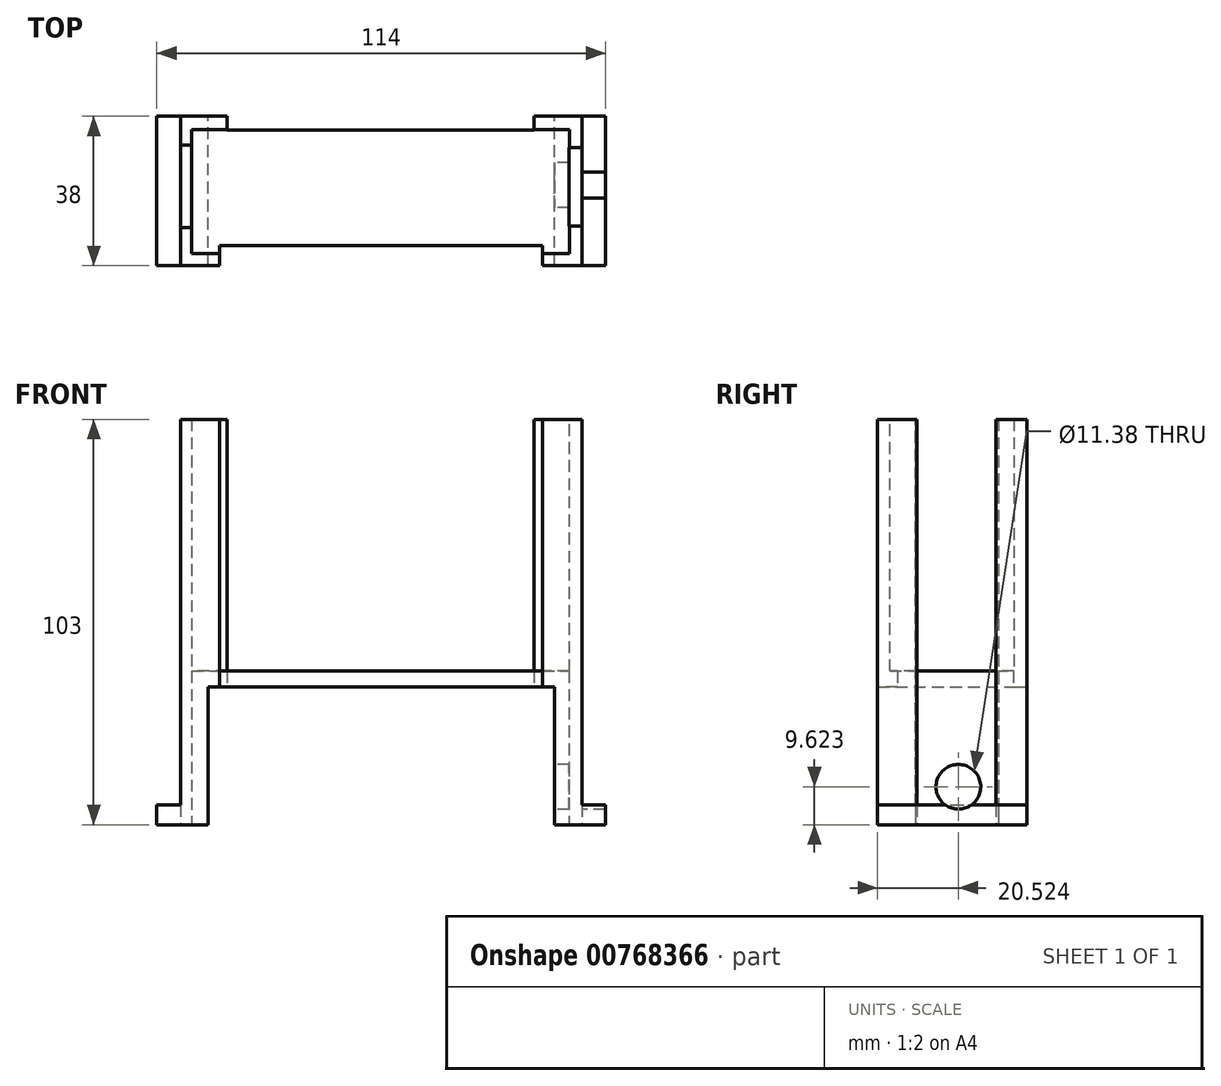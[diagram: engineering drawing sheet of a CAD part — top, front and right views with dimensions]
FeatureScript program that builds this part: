
annotation { "Feature Type Name" : "Feature", "Feature Type Description" : "" }
export const myFeature = defineFeature(function(context is Context, id is Id, definition is map)
    precondition{}
    {
        {
            var Q0;
            Q0=qCreatedBy(makeId("Front.planeOp"),FACE);
            var sketch = newSketch(context, id + "F0", { "sketchPlane" : qUnion([Q0])});
            skLineSegment(sketch, "E0", {"start": v(-44, 0) * mm, "end": v(-57, 0) * mm});
            skLineSegment(sketch, "E1", {"start": v(-57, 0) * mm, "end": v(-57, 5) * mm});
            skLineSegment(sketch, "E2", {"start": v(-57, 5) * mm, "end": v(-51, 5) * mm});
            skLineSegment(sketch, "E3", {"start": v(-51, 5) * mm, "end": v(-51, 103) * mm});
            skLineSegment(sketch, "E4", {"start": v(-51, 103) * mm, "end": v(0, 103) * mm});
            skLineSegment(sketch, "E5", {"start": v(-44, 0) * mm, "end": v(-44, 35) * mm});
            skLineSegment(sketch, "E6", {"start": v(-44, 35) * mm, "end": v(0, 35) * mm});
            skLineSegment(sketch, "E7", {"start": v(0, -35.05) * mm, "end": v(0, 128.52) * mm, "construction": true});
            skLineSegment(sketch, "E8.MirrorCS", {"start": v(51, 103) * mm, "end": v(0, 103) * mm});
            skLineSegment(sketch, "E9.MirrorCS", {"start": v(51, 5) * mm, "end": v(51, 103) * mm});
            skLineSegment(sketch, "E10.MirrorCS", {"start": v(44, 35) * mm, "end": v(0, 35) * mm});
            skLineSegment(sketch, "E11.MirrorCS", {"start": v(44, 0) * mm, "end": v(44, 35) * mm});
            skLineSegment(sketch, "E12.MirrorCS", {"start": v(57, 5) * mm, "end": v(51, 5) * mm});
            skLineSegment(sketch, "E13.MirrorCS", {"start": v(57, 0) * mm, "end": v(57, 5) * mm});
            skLineSegment(sketch, "E14.MirrorCS", {"start": v(44, 0) * mm, "end": v(57, 0) * mm});
            skSolve(sketch);
        }
        {
            var Q0;
            Q0 = qSketchRegion(id + "F0", true);
            extrude(context, id + "F1", {"entities" : qUnion([Q0]), "depth" : 38 * mm, "offsetDistance" : 25 * mm});
        }
        {
            var Q0;
            Q0=qCreatedBy(makeId("Top.planeOp"),FACE);
            var sketch = newSketch(context, id + "F2", { "sketchPlane" : qUnion([Q0])});
            skLineSegment(sketch, "E15", {"start": v(-48.13, -3.4) * mm, "end": v(-48.13, -34.9) * mm});
            skLineSegment(sketch, "E16", {"start": v(-48.13, -34.9) * mm, "end": v(47.87, -34.9) * mm});
            skLineSegment(sketch, "E17", {"start": v(47.87, -34.9) * mm, "end": v(47.87, -3.4) * mm});
            skLineSegment(sketch, "E18", {"start": v(47.87, -3.4) * mm, "end": v(-48.13, -3.4) * mm});
            skSolve(sketch);
        }
        {
            var Q0;
            Q0 = qSketchRegion(id + "F2", true);
            extrude(context, id + "F3", {"entities" : qUnion([Q0]), "operationType" : NewBodyOperationType.ADD, "depth" : 120 * mm, "offsetDistance" : 25 * mm});
        }
        {
            var Q0;
            Q0=makeQuery(id+"F3.opExtrude","CAP_FACE",FACE,{"disambiguationData":[OSD([sQuery(id+"F2.wireOp",EDGE,"E15"),sQuery(id+"F2.wireOp",EDGE,"E16"),sQuery(id+"F2.wireOp",EDGE,"E17"),sQuery(id+"F2.wireOp",EDGE,"E18")])],"isStart":false});
            extrude(context, id + "F4", {"entities" : qUnion([Q0]), "operationType" : NewBodyOperationType.REMOVE, "oppositeDirection" : true, "depth" : 81 * mm, "offsetDistance" : 25 * mm});
        }
        {
            var Q0;
            {var subQ0=sQuery(id+"F2.wireOp",EDGE,"E16");Q0=makeQuery(id+"F3.boolean.opBoolean","SPLIT",FACE,{"disambiguationData":[TD([makeQuery(id+"F1.opExtrude","SWEPT_FACE",FACE,{"disambiguationData":[OSD([sQuery(id+"F0.wireOp",EDGE,"E0")])]})])],"derivedFrom":makeQuery(id+"F3.opExtrude","SWEPT_FACE",FACE,{"disambiguationData":[OSD([subQ0])]})});}
            extrude(context, id + "F5", {"entities" : qUnion([Q0]), "operationType" : NewBodyOperationType.REMOVE, "oppositeDirection" : true, "depth" : 50 * mm, "offsetDistance" : 25 * mm});
        }
        {
            var Q0;
            Q0=qCreatedBy(makeId("Top.planeOp"),FACE);
            var sketch = newSketch(context, id + "F6", { "sketchPlane" : qUnion([Q0])});
            skLineSegment(sketch, "E19", {"start": v(-41, -32.9) * mm, "end": v(-41, -41.33) * mm});
            skLineSegment(sketch, "E20", {"start": v(-41, -41.33) * mm, "end": v(41, -41.33) * mm});
            skLineSegment(sketch, "E21", {"start": v(41, -41.33) * mm, "end": v(41, -32.9) * mm});
            skLineSegment(sketch, "E22", {"start": v(41, -32.9) * mm, "end": v(-41, -32.9) * mm});
            skSolve(sketch);
        }
        {
            var Q0;
            Q0 = qSketchRegion(id + "F6", true);
            extrude(context, id + "F7", {"entities" : qUnion([Q0]), "operationType" : NewBodyOperationType.REMOVE, "depth" : 120 * mm, "offsetDistance" : 25 * mm});
        }
        {
            var Q0;
            Q0=qCreatedBy(makeId("Top.planeOp"),FACE);
            var sketch = newSketch(context, id + "F8", { "sketchPlane" : qUnion([Q0])});
            skLineSegment(sketch, "E23.bottom", {"start": v(47.8, -7.95) * mm, "end": v(51.08, -7.95) * mm});
            skLineSegment(sketch, "E23.top", {"start": v(47.8, -27.95) * mm, "end": v(51.08, -27.95) * mm});
            skLineSegment(sketch, "E23.left", {"start": v(47.8, -7.95) * mm, "end": v(47.8, -27.95) * mm});
            skLineSegment(sketch, "E23.right", {"start": v(51.08, -7.95) * mm, "end": v(51.08, -27.95) * mm});
            skSolve(sketch);
        }
        {
            var Q0;
            Q0 = qSketchRegion(id + "F8", true);
            extrude(context, id + "F9", {"entities" : qUnion([Q0]), "operationType" : NewBodyOperationType.ADD, "depth" : 120 * mm, "offsetDistance" : 25 * mm});
        }
        {
            var Q0;
            Q0 = qSketchRegion(id + "F8", true);
            extrude(context, id + "F10", {"entities" : qUnion([Q0]), "operationType" : NewBodyOperationType.REMOVE, "depth" : 120 * mm, "offsetDistance" : 25 * mm});
        }
        {
            var Q0;
            Q0=qCreatedBy(makeId("Top.planeOp"),FACE);
            var sketch = newSketch(context, id + "F11", { "sketchPlane" : qUnion([Q0])});
            skLineSegment(sketch, "E24.bottom", {"start": v(-39.12, 0) * mm, "end": v(38.88, 0) * mm});
            skLineSegment(sketch, "E24.top", {"start": v(-39.12, -3.46) * mm, "end": v(38.88, -3.46) * mm});
            skLineSegment(sketch, "E24.left", {"start": v(-39.12, 0) * mm, "end": v(-39.12, -3.46) * mm});
            skLineSegment(sketch, "E24.right", {"start": v(38.88, 0) * mm, "end": v(38.88, -3.46) * mm});
            skSolve(sketch);
        }
        {
            var Q0;
            Q0 = qSketchRegion(id + "F11", true);
            extrude(context, id + "F12", {"entities" : qUnion([Q0]), "operationType" : NewBodyOperationType.ADD, "depth" : 120 * mm, "offsetDistance" : 25 * mm});
        }
        {
            var Q0;
            Q0 = qSketchRegion(id + "F11", true);
            extrude(context, id + "F13", {"entities" : qUnion([Q0]), "operationType" : NewBodyOperationType.REMOVE, "depth" : 120 * mm, "offsetDistance" : 25 * mm});
        }
        {
            var Q0;
            Q0=qCreatedBy(makeId("Top.planeOp"),FACE);
            var sketch = newSketch(context, id + "F14", { "sketchPlane" : qUnion([Q0])});
            skLineSegment(sketch, "E25.bottom", {"start": v(-51, -7.31) * mm, "end": v(-48.09, -7.31) * mm});
            skLineSegment(sketch, "E25.top", {"start": v(-51, -28.31) * mm, "end": v(-48.09, -28.31) * mm});
            skLineSegment(sketch, "E25.left", {"start": v(-51, -7.31) * mm, "end": v(-51, -28.31) * mm});
            skLineSegment(sketch, "E25.right", {"start": v(-48.09, -7.31) * mm, "end": v(-48.09, -28.31) * mm});
            skSolve(sketch);
        }
        {
            var Q0;
            Q0 = qSketchRegion(id + "F14", true);
            extrude(context, id + "F15", {"entities" : qUnion([Q0]), "operationType" : NewBodyOperationType.ADD, "depth" : 120 * mm, "offsetDistance" : 25 * mm});
        }
        {
            var Q0;
            Q0 = qSketchRegion(id + "F14", true);
            extrude(context, id + "F16", {"entities" : qUnion([Q0]), "operationType" : NewBodyOperationType.REMOVE, "depth" : 120 * mm, "offsetDistance" : 25 * mm});
        }
        {
            var Q0;
            Q0=qCreatedBy(makeId("Right.planeOp"),FACE);
            var sketch = newSketch(context, id + "F17", { "sketchPlane" : qUnion([Q0])});
            skCircle(sketch, "E26", {"center": v(-17.48, 9.62) * mm, "radius": 5.69 * mm});
            skSolve(sketch);
        }
        {
            var Q0;
            Q0 = qSketchRegion(id + "F17", true);
            extrude(context, id + "F18", {"entities" : qUnion([Q0]), "operationType" : NewBodyOperationType.ADD, "depth" : 120 * mm, "offsetDistance" : 25 * mm});
        }
        {
            var Q0;
            Q0 = qSketchRegion(id + "F17", true);
            extrude(context, id + "F19", {"entities" : qUnion([Q0]), "operationType" : NewBodyOperationType.REMOVE, "depth" : 120 * mm, "offsetDistance" : 25 * mm});
        }
    });
